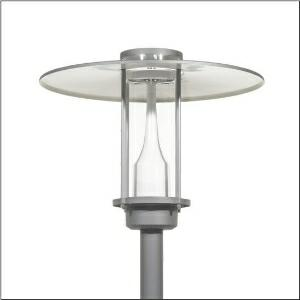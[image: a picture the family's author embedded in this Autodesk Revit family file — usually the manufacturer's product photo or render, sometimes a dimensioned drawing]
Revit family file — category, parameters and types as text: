
# Revit family: city-light_plus_iq___p1_0a_5xa5275bf14h_49c5
name_source: partatom
category: Lighting Fixtures
units: mm (PartAtom-declared; Revit-internal decimal feet)

## family parameters
Cut with Voids When Loaded = No
Host = Face
Light Source = No
Part Type = Normal
Room Calculation Point = No
Round Connector Dimension = Use Diameter
Shared = No

## types (1)
- --- (1 x LED, 1440 lm, 12.9 W, 2200K)
    Apparent Load = 13 VA
    CIE Flux Codes = 32 61 90 96 100
    Color Rendering = 70
    Color Temperature = 2200K
    Default Elevation = 1800 mm
    Description = City-Light Plus iQ, mast luminaire, Module 540 iQ-SR, primary light control with 3 zone facetted reflector, of plastic, silver coated, highly specular, structured, primary optical cover: cover, of PMMA, transparent, light distribution: P1.0a, light emission: direct distribution, primary light characteristic: strongly asymmetric, installation type: post-top, LED, High Power LED, rated luminous flux: 1.440lm, luminous efficacy: 112lm/W, light colour: 722, colour temperature: 2200K, control gear: iQ Street-Remote, control: pre-setting: logarithmic dimming characteristic, Street-Remote, Auto-Match, Temp-Guard, Lumen-Switch, Night-Set, Smart-Wire, Light-Fading, Desk-Remote (wireless, voltage-free reading and setting of iQ features in the workshop via application-optimized NFC function/RFID function), optimised constant luminous flux control (CLO 2.0), with terminal, 6-pole, max. 2.5mm², mains connection: 230..240V, AC, 50/60Hz, start of lifetime: 13W, end of service life: 13W, reduction: 6W, luminaire housing, upper part, of glass-fibre reinforced polyester, coated, Siteco® metallic grey (DB 702S), diameter: 750mm, height: 590mm, spigot size: d x l = 76 x 70mm (post-top) | with reducer (optional accessory) 60 x 70mm, mounting height: 3..5m, post-top mast mounting element, of diecast aluminium, coated, Siteco® metallic grey (DB 702S), Module 540 iQ-SR, traffic white (RAL 9016), equipment: standard, protection rating (complete): IP65, insulation class (complete): insulation class II (safety insulation), certification: CE, ENEC, VDE, packaging unit: 1 piece

Light Distribution: P1.0a
    Height = 590 mm
    Lamp = 1 x LED
    Lamp Light Flux = 1440 lm
    Lamp Power = 12.9 W
    Lamp count = 1
    Length = 750 mm
    Luminous efficacy = 112 lm/W
    Manufacturer = Siteco
    ModVariant = No
    Model = 5XA5275BF14H
    Number of Poles = 1
    OnlyDefault = Yes
    Power Factor = 1
    Product Name = City-Light Plus iQ | P1.0a
    Product group = mast luminaire | pylon top
    ProductGroupID = 6100
    Protection Class = Protection class II
    Protection Degree = IP 65
    RLX_Detail_Level = 1
    RLX_Emergency_Light_Flux = 0 lm
    RLX_Emergency_Type = 0
    RLX_Emergency_Type_DB = No
    RlxData = <blob elided: 60769 chars, md5=4788d36d>
    Socket = socket
    Standby Power = 0 W
    System Light Flux = 1440 lm
    System Power = 13 W
    Type Comments = factory setting: luminous flux: 100 % | dim-lin: 254 | 516 mA
    Type Image = l_1006456.jpg
    URL = http://relux.com
    VarID = @adj_160042
    Voltage = 0 V
    Weight = 0.00 kg
    Width = 0 mm  [stored 0 ft]

note: [stored X ft] marks values corroborated as IEEE doubles in the binary element streams (Revit-internal decimal feet)

## geometry (parser evidence)
native form markers: Blend x4, Sweep x11
no freeform markers — native parametric forms only
